FCSTD DOCUMENT  (FreeCAD 0.20R29603 (Git))
Label: layout
License: All rights reserved
LicenseURL: http://en.wikipedia.org/wiki/All_rights_reserved
objects: Sketcher::SketchObject×4, Spreadsheet::Sheet×1
note: 4 computed .brp shape members not serialized (recipe doc carries the construction recipe); baked Part::Feature solids carry a one-line shape summary decoded from their .brp

FEATURE [Spreadsheet::Sheet] Spreadsheet  label="Constants"
  cells = B1=X; C1=Y; D1=Angle; E1=Variance; A2=Far index; C2(FarIndexY)==3 mm; A3=Index; B3(IndexX)==20 mm; C3(IndexY)==8 mm; A4=Ring; B4(RingX)==18 mm; C4(RingY)==10 mm; A5=Far ring; C5(FarRingY)==2 mm; A6=Wide ring; C6(WideRingY)==2 mm; A7=Pinky; B7(PinkyX)==37 mm; C7(PinkyY)==31 mm; A8=Far pinky; B8(FarPinkyX)==35 mm; C8(FarPinkyY)==33 mm; E8(FarPinkyVariance)==1 mm; A9=Thumb; B9(ThumbX)==48 mm; C9(ThumbY)==49 mm; D9(ThumbAngle)==5 deg; A10=LeftThumb; C10(LeftThumbY)==3 mm; D10(LeftThumbAngle)==15 deg; A11=RightThumb; C11(RightThumbY)==3 mm; D11(RightThumbAngle)==15 deg; A12=Numpad; C12(NumpadY)==5 mm; D12(NumpadAngle)==10 deg; B15=Width; C15=Height; A16=Key size; B16(KeyWidth)==18 mm; C16(KeyHeight)==17 mm; A17=Switch hole size; B17(SwitchHoleSize)==14 mm; A18=Edge padding; B18(EdgePaddingWidth)==(KeyWidth - SwitchHoleSize) / 2; C18(EdgePaddingHeight)==1.5 mm; A19=Numpad spacing; B19(NumpadSpacingWidth)==1 mm; C19(NumpadSpacingHeight)==3 mm; A20=Component spacing; B20(ComponentSpacing)==0.5 mm; A21=Corner raidus; B21(CornerRadius)==1 mm; A22=Micro controller size; B22(MicroControllerWidth)==17.78 mm; C22(MicroControllerHeight)==33.02 mm; A23=TRRS size; B23(TRRSWidth)==6.1 mm; C23(TRRSHeight)==12.45 mm; D23(TRRSFullHeight)==100 mm; A24=LED diameter; B24(LEDDiameter)==3.175 mm; A25=Breakaway gap; B25(BreakawayGap)==1 mm; A26=Breakaway width; B26(BreakawayWidth)==8 mm; A27=Breakway margin; B27(BreakawayMargin)==12 mm
FEATURE [Sketcher::SketchObject] Sketch  label="Grid"
  FullyConstrained = true
  expr: Constraints[107] = 2 * Spreadsheet.KeyHeight
  expr: Constraints[108] = <<Constants>>.KeyHeight
  expr: Constraints[109] = Spreadsheet.KeyWidth
  expr: Constraints[10] = 3 * Spreadsheet.KeyHeight
  expr: Constraints[110] = Spreadsheet.KeyWidth
  expr: Constraints[111] = Spreadsheet.FarRingY
  expr: Constraints[112] = Spreadsheet.FarPinkyY
  expr: Constraints[113] = Spreadsheet.FarPinkyX
  expr: Constraints[114] = <<Constants>>.ThumbAngle
  expr: Constraints[122] = <<Constants>>.RightThumbAngle
  expr: Constraints[123] = <<Constants>>.KeyWidth
  expr: Constraints[124] = <<Constants>>.KeyHeight
  expr: Constraints[125] = Spreadsheet.RightThumbY + <<Constants>>.KeyHeight
  expr: Constraints[133] = <<Constants>>.KeyHeight
  expr: Constraints[134] = <<Constants>>.KeyWidth
  expr: Constraints[136] = Spreadsheet.LeftThumbY
  expr: Constraints[137] = <<Constants>>.LeftThumbAngle
  expr: Constraints[147] = <<Constants>>.KeyHeight
  expr: Constraints[148] = <<Constants>>.KeyWidth
  expr: Constraints[156] = <<Constants>>.FarIndexY
  expr: Constraints[157] = Spreadsheet.IndexY
  expr: Constraints[158] = Spreadsheet.IndexX
  expr: Constraints[19] = Spreadsheet.KeyWidth
  expr: Constraints[20] = 3 * Spreadsheet.KeyHeight
  expr: Constraints[28] = Spreadsheet.KeyWidth
  expr: Constraints[29] = 3 * Spreadsheet.KeyHeight
  expr: Constraints[40] = Spreadsheet.KeyWidth
  expr: Constraints[41] = 3 * Spreadsheet.KeyHeight
  expr: Constraints[46] = Spreadsheet.KeyWidth
  expr: Constraints[47] = Spreadsheet.KeyHeight
  expr: Constraints[64] = Spreadsheet.KeyWidth
  expr: Constraints[65] = Spreadsheet.KeyHeight
  expr: Constraints[70] = Spreadsheet.KeyWidth
  expr: Constraints[76] = Spreadsheet.KeyHeight
  expr: Constraints[79] = Spreadsheet.RingY
  expr: Constraints[80] = Spreadsheet.PinkyY
  expr: Constraints[82] = Spreadsheet.ThumbY
  expr: Constraints[83] = Spreadsheet.PinkyX
  expr: Constraints[91] = Spreadsheet.KeyWidth
  expr: Constraints[92] = 2 * <<Constants>>.KeyHeight
  expr: Constraints[94] = Spreadsheet.ThumbX
  expr: Constraints[96] = Spreadsheet.RingX
  expr: Constraints[9] = Spreadsheet.KeyWidth
  sketch-geometry (58):
    g0: LineSegment StartX=-9 StartY=25.5 StartZ=0 EndX=9 EndY=25.5 EndZ=0
    g1: LineSegment StartX=9 StartY=25.5 StartZ=0 EndX=9 EndY=-25.5 EndZ=0
    g2: LineSegment StartX=9 StartY=-25.5 StartZ=0 EndX=-9 EndY=-25.5 EndZ=0
    g3: LineSegment StartX=-9 StartY=-25.5 StartZ=0 EndX=-9 EndY=25.5 EndZ=0
    g4: LineSegment StartX=-11 StartY=17.5 StartZ=0 EndX=-29 EndY=17.5 EndZ=0
    g5: LineSegment StartX=-29 StartY=17.5 StartZ=0 EndX=-29 EndY=-33.5 EndZ=0
    g6: LineSegment StartX=-29 StartY=-33.5 StartZ=0 EndX=-11 EndY=-33.5 EndZ=0
    g7: LineSegment StartX=-11 StartY=-33.5 StartZ=0 EndX=-11 EndY=17.5 EndZ=0
    g8: LineSegment StartX=9 StartY=-35.5 StartZ=0 EndX=9 EndY=15.5 EndZ=0
    g9: LineSegment StartX=9 StartY=15.5 StartZ=0 EndX=27 EndY=15.5 EndZ=0
    g10: LineSegment StartX=27 StartY=15.5 StartZ=0 EndX=27 EndY=-35.5 EndZ=0
    g11: LineSegment StartX=27 StartY=-35.5 StartZ=0 EndX=9 EndY=-35.5 EndZ=0
    g12: GeomPoint X=18 Y=-10 Z=0
    g13: LineSegment StartX=-29 StartY=14.5 StartZ=0 EndX=-47 EndY=14.5 EndZ=0
    g14: LineSegment StartX=-47 StartY=14.5 StartZ=0 EndX=-47 EndY=-36.5 EndZ=0
    g15: LineSegment StartX=-47 StartY=-36.5 StartZ=0 EndX=-29 EndY=-36.5 EndZ=0
    g16: LineSegment StartX=-29 StartY=-36.5 StartZ=0 EndX=-29 EndY=-33.5 EndZ=0
    g17: LineSegment StartX=28 StartY=-22.5 StartZ=0 EndX=28 EndY=-39.5 EndZ=0
    g18: LineSegment StartX=46 StartY=-39.5 StartZ=0 EndX=46 EndY=-22.5 EndZ=0
    g19: LineSegment StartX=46 StartY=-22.5 StartZ=0 EndX=28 EndY=-22.5 EndZ=0
    g20: LineSegment StartX=46 StartY=-41.5 StartZ=0 EndX=64 EndY=-41.5 EndZ=0
    g21: GeomPoint X=37 Y=-31 Z=0
    g22: GeomPoint X=-48 Y=-49 Z=0
    g23: LineSegment StartX=-38.2934 StartY=-56.6833 StartZ=0 EndX=-34.8205 EndY=-36.9871 EndZ=0
    g24: LineSegment StartX=46 StartY=-39.5 StartZ=0 EndX=46 EndY=-41.5 EndZ=0
    g25: GeomPoint X=35 Y=-48 Z=0
    g26: LineSegment StartX=46 StartY=-39.5 StartZ=0 EndX=28 EndY=-39.5 EndZ=0
    g27: LineSegment StartX=28 StartY=-39.5 StartZ=0 EndX=26 EndY=-39.5 EndZ=0
    g28: LineSegment StartX=26 StartY=-39.5 StartZ=0 EndX=26 EndY=-56.5 EndZ=0
    g29: LineSegment StartX=26 StartY=-56.5 StartZ=0 EndX=44 EndY=-56.5 EndZ=0
    g30: LineSegment StartX=44 StartY=-56.5 StartZ=0 EndX=44 EndY=-39.5 EndZ=0
    g31: LineSegment StartX=-38.2934 StartY=-56.6833 StartZ=0 EndX=-56.2249 EndY=-58.2521 EndZ=0
    g32: LineSegment StartX=-56.2249 StartY=-58.2521 StartZ=0 EndX=-57.7066 EndY=-41.3167 EndZ=0
    g33: LineSegment StartX=-57.7066 StartY=-41.3167 StartZ=0 EndX=-39.7751 EndY=-39.7479 EndZ=0
    g34: GeomPoint X=-48 Y=-49 Z=0
    g35: LineSegment StartX=-38.2934 StartY=-56.6833 StartZ=0 EndX=-39.7751 EndY=-39.7479 EndZ=0
    g36: GeomPoint X=55 Y=-33 Z=0
    g37: LineSegment StartX=46 StartY=-22.5 StartZ=0 EndX=46 EndY=-7.5 EndZ=0
    g38: LineSegment StartX=46 StartY=-7.5 StartZ=0 EndX=64 EndY=-7.5 EndZ=0
    g39: LineSegment StartX=64 StartY=-7.5 StartZ=0 EndX=64 EndY=-41.5 EndZ=0
    g40: LineSegment StartX=27 StartY=13.5 StartZ=0 EndX=45 EndY=13.5 EndZ=0
    g41: LineSegment StartX=45 StartY=13.5 StartZ=0 EndX=45 EndY=-20.5 EndZ=0
    g42: LineSegment StartX=45 StartY=-20.5 StartZ=0 EndX=27 EndY=-20.5 EndZ=0
    g43: LineSegment StartX=45 StartY=-7.5 StartZ=0 EndX=63 EndY=-7.5 EndZ=0
    g44: LineSegment StartX=63 StartY=-7.5 StartZ=0 EndX=63 EndY=9.5 EndZ=0
    g45: LineSegment StartX=63 StartY=9.5 StartZ=0 EndX=45 EndY=9.5 EndZ=0
    g46: LineSegment StartX=-34.8205 StartY=-36.9871 StartZ=0 EndX=-17.0939 EndY=-40.1128 EndZ=0
    g47: LineSegment StartX=-17.0939 StartY=-40.1128 StartZ=0 EndX=-20.0459 EndY=-56.8545 EndZ=0
    g48: LineSegment StartX=-20.0459 StartY=-56.8545 StartZ=0 EndX=-37.7725 EndY=-53.7288 EndZ=0
    g49: LineSegment StartX=-61.0132 StartY=-45.0964 StartZ=0 EndX=-55.1989 EndY=-61.0711 EndZ=0
    g50: LineSegment StartX=-55.1989 StartY=-61.0711 StartZ=0 EndX=-72.1133 EndY=-67.2275 EndZ=0
    g51: LineSegment StartX=-72.1133 StartY=-67.2275 StartZ=0 EndX=-77.9277 EndY=-51.2527 EndZ=0
    g52: LineSegment StartX=-77.9277 StartY=-51.2527 StartZ=0 EndX=-61.0132 EndY=-45.0964 EndZ=0
    g53: LineSegment StartX=46 StartY=-41.5 StartZ=0 EndX=44 EndY=-41.5 EndZ=0
    g54: LineSegment StartX=44 StartY=-56.5 StartZ=0 EndX=44 EndY=-58.5 EndZ=0
    g55: LineSegment StartX=44 StartY=-58.5 StartZ=0 EndX=62 EndY=-58.5 EndZ=0
    g56: LineSegment StartX=62 StartY=-58.5 StartZ=0 EndX=62 EndY=-41.5 EndZ=0
    g57: GeomPoint X=64 Y=-24.5 Z=0
  constraints (160):
    c: Coincident(g0,g1)
    c: Coincident(g1,g2)
    c: Coincident(g2,g3)
    c: Coincident(g3,g0)
    c: Horizontal(g0)
    c: Horizontal(g2)
    c: Vertical(g1)
    c: Vertical(g3)
    c: Symmetric(g0,g1,g-1)
    c: Distance(g0) = 18
    c: Distance(g1) = 51
    c: Coincident(g4,g5)
    c: Coincident(g5,g6)
    c: Coincident(g6,g7)
    c: Coincident(g7,g4)
    c: Horizontal(g4)
    c: Horizontal(g6)
    c: Vertical(g5)
    c: Vertical(g7)
    c: Distance(g4) = 18
    c: Distance(g7) = 51
    c: Coincident(g9,g8)
    c: Coincident(g10,g9)
    c: Coincident(g11,g10)
    c: Coincident(g11,g8)
    c: Perpendicular(g8,g9)
    c: Perpendicular(g10,g9)
    c: Perpendicular(g11,g8)
    c: Distance(g9) = 18
    c: Distance(g10) = 51
    c: Symmetric(g8,g10,g12)
    c: PointOnObject(g13,g5)
    c: Horizontal(g13)
    c: Coincident(g14,g13)
    c: Vertical(g14)
    c: Coincident(g15,g14)
    c: Horizontal(g15)
    c: Coincident(g16,g15)
    c: Coincident(g16,g5)
    c: Vertical(g16)
    c: Distance(g13) = 18
    c: Distance(g14) = 51
    c: Coincident(g19,g18)
    c: Coincident(g19,g17)
    c: Perpendicular(g17,g19)
    c: Perpendicular(g18,g19)
    c: Distance(g19) = 18
    c: Distance(g18) = 17
    c: Coincident(g24,g20)
    c: Perpendicular(g20,g24)
    c: Symmetric(g17,g18,g21)
    c: Coincident(g18,g24)
    c: Coincident(g26,g18)
    c: Coincident(g26,g17)
    c: Perpendicular(g26,g18)
    c: Coincident(g27,g17)
    c: Coincident(g28,g27)
    c: Coincident(g29,g28)
    c: Coincident(g30,g29)
    c: PointOnObject(g30,g26)
    c: Perpendicular(g30,g26)
    c: Perpendicular(g29,g30)
    c: Perpendicular(g28,g29)
    c: Perpendicular(g27,g28)
    c: Distance(g29) = 18
    c: Distance(g30) = 17
    c: Symmetric(g27,g29,g25)
    c: Coincident(g32,g31)
    c: Coincident(g33,g32)
    c: Symmetric(g32,g31,g34)
    c: Distance(g33) = 18
    c: Perpendicular(g32,g31)
    c: Coincident(g35,g31)
    c: Coincident(g35,g33)
    c: Perpendicular(g31,g35)
    c: Perpendicular(g33,g32)
    c: Distance(g35) = 17
    c: Coincident(g22,g34)
    c: Coincident(g23,g31)
    c: DistanceY(g12,g-1) = 10
    c: DistanceY(g21,g-1) = 31
    c: Perpendicular(g26,g24)
    c: DistanceY(g22,g-1) = 49
    c: DistanceX(g-1,g21) = 37
    c: Coincident(g37,g18)
    c: Coincident(g38,g37)
    c: Coincident(g39,g38)
    c: Coincident(g39,g20)
    c: Perpendicular(g20,g39)
    c: Perpendicular(g38,g37)
    c: Perpendicular(g39,g38)
    c: Distance(g38) = 18
    c: Distance(g39) = 34
    c: Angle(g17,g-2) = 0
    c: DistanceX(g22,g-1) = 48
    c: Horizontal(g9)
    c: DistanceX(g-1,g12) = 18
    c: PointOnObject(g40,g10)
    c: Coincident(g41,g40)
    c: Coincident(g42,g41)
    c: PointOnObject(g42,g10)
    c: Coincident(g44,g43)
    c: Coincident(g45,g44)
    c: PointOnObject(g45,g41)
    c: Perpendicular(g10,g40)
    c: Perpendicular(g41,g40)
    c: Perpendicular(g42,g41)
    c: Distance(g41) = 34
    c: Distance(g44) = 17
    c: Distance(g40) = 18
    c: Distance(g45) = 18
    c: DistanceY(g40,g9) = 2
    c: DistanceY(g36,g-1) = 33
    c: DistanceX(g-1,g25) = 35
    c: Angle(g-2,g35) = 0.0872665
    c: Coincident(g46,g23)
    c: Coincident(g47,g46)
    c: Coincident(g48,g47)
    c: PointOnObject(g48,g23)
    c: Perpendicular(g46,g23)
    c: Perpendicular(g47,g46)
    c: Perpendicular(g48,g47)
    c: Angle(g23,g35) = 0.261799
    c: Distance(g46) = 18
    c: Distance(g47) = 17
    c: Distance(g23) = 20
    c: Coincident(g50,g49)
    c: Coincident(g51,g50)
    c: Coincident(g52,g51)
    c: Coincident(g52,g49)
    c: Perpendicular(g52,g49)
    c: Perpendicular(g51,g52)
    c: Perpendicular(g50,g49)
    c: Distance(g49) = 17
    c: Distance(g52) = 18
    c: PointOnObject(g31,g49)
    c: Distance(g31,g50) = 3
    c: Angle(g32,g49) = 0.261799
    c: Coincident(g53,g20)
    c: PointOnObject(g53,g30)
    c: Horizontal(g53)
    c: Coincident(g54,g29)
    c: Vertical(g54)
    c: Coincident(g55,g54)
    c: Horizontal(g55)
    c: PointOnObject(g56,g20)
    c: Vertical(g56)
    c: Distance(g56) = 17
    c: Distance(g55) = 18
    c: Coincident(g56,g55)
    c: PointOnObject(g43,g41)
    c: Horizontal(g45)
    c: Horizontal(g43)
    c: Vertical(g44)
    c: Symmetric(g20,g57,g36)
    c: Symmetric(g38,g20,g57)
    c: DistanceY(g13,g4) = 3
    c: DistanceY(g4,g0) = 8
    c: DistanceX(g4,g0) = 20
    c: PointOnObject(g43,g38)
FEATURE [Sketcher::SketchObject] Sketch001  label="Edge"
  FullyConstrained = true
  expr: Constraints[102] = <<Constants>>.KeyWidth + <<Constants>>.EdgePaddingWidth - <<Constants>>.CornerRadius
  expr: Constraints[105] = <<Constants>>.IndexX + 1.5 * <<Constants>>.KeyWidth + <<Constants>>.EdgePaddingWidth
  expr: Constraints[107] = 1.5 * <<Constants>>.KeyHeight - <<Constants>>.IndexY + <<Constants>>.EdgePaddingHeight
  expr: Constraints[11] = <<Constants>>.CornerRadius
  expr: Constraints[12] = <<Constants>>.CornerRadius
  expr: Constraints[13] = <<Constants>>.PinkyX + 1.5 * <<Constants>>.KeyWidth + <<Constants>>.EdgePaddingWidth
  expr: Constraints[16] = <<Constants>>.CornerRadius
  expr: Constraints[17] = <<Constants>>.FarPinkyY + <<Constants>>.FarPinkyVariance + 1.5 * <<Constants>>.KeyHeight + <<Constants>>.EdgePaddingHeight
  expr: Constraints[19] = <<Constants>>.CornerRadius
  expr: Constraints[1] = <<Constants>>.KeyHeight * 1.5 + <<Constants>>.EdgePaddingHeight
  expr: Constraints[23] = Spreadsheet.MicroControllerHeight + 2 * <<Constants>>.ComponentSpacing
  expr: Constraints[24] = <<Constants>>.CornerRadius
  expr: Constraints[28] = <<Constants>>.CornerRadius
  expr: Constraints[32] = <<Constants>>.CornerRadius
  expr: Constraints[37] = <<Constants>>.CornerRadius
  expr: Constraints[3] = <<Constants>>.KeyWidth / 2 + <<Constants>>.EdgePaddingWidth
  expr: Constraints[42] = <<Constants>>.ThumbX
  expr: Constraints[43] = <<Constants>>.ThumbY
  expr: Constraints[45] = <<Constants>>.KeyHeight
  expr: Constraints[46] = <<Constants>>.KeyWidth
  expr: Constraints[47] = <<Constants>>.ThumbAngle
  expr: Constraints[49] = <<Constants>>.LeftThumbAngle
  expr: Constraints[50] = <<Constants>>.LeftThumbY
  expr: Constraints[51] = <<Constants>>.EdgePaddingHeight
  expr: Constraints[52] = <<Constants>>.EdgePaddingHeight
  expr: Constraints[53] = <<Constants>>.KeyHeight
  expr: Constraints[54] = <<Constants>>.CornerRadius
  expr: Constraints[55] = <<Constants>>.CornerRadius
  expr: Constraints[56] = <<Constants>>.CornerRadius
  expr: Constraints[57] = <<Constants>>.CornerRadius
  expr: Constraints[5] = <<Constants>>.KeyWidth / 2 + <<Constants>>.EdgePaddingWidth
  expr: Constraints[65] = <<Constants>>.TRRSHeight + 2 * <<Constants>>.ComponentSpacing
  expr: Constraints[6] = <<Constants>>.CornerRadius
  expr: Constraints[72] = <<Constants>>.CornerRadius
  expr: Constraints[73] = <<Constants>>.CornerRadius
  expr: Constraints[76] = <<Constants>>.CornerRadius
  expr: Constraints[83] = Spreadsheet.BreakawayMargin - Spreadsheet.BreakawayGap / 2 - <<Constants>>.CornerRadius
  expr: Constraints[84] = Spreadsheet.BreakawayMargin - Spreadsheet.BreakawayGap / 2 - <<Constants>>.CornerRadius
  expr: Constraints[87] = Spreadsheet.BreakawayWidth + Spreadsheet.BreakawayGap
  expr: Constraints[88] = Spreadsheet.BreakawayWidth + Spreadsheet.BreakawayGap
  expr: Constraints[95] = <<Constants>>.MicroControllerWidth + 2 * <<Constants>>.ComponentSpacing
  expr: Constraints[97] = <<Constants>>.TRRSWidth + <<Constants>>.ComponentSpacing
  sketch-geometry (42):
    g0: LineSegment StartX=10 StartY=27 StartZ=0 EndX=-10 EndY=27 EndZ=0
    g1: LineSegment StartX=-11 StartY=20 StartZ=0 EndX=-11 EndY=26 EndZ=0
    g2: LineSegment StartX=11 StartY=26 StartZ=0 EndX=11 EndY=20 EndZ=0
    g3: ArcOfCircle CenterX=-10 CenterY=26 CenterZ=0 NormalX=0 NormalY=0 NormalZ=1 AngleXU=0 Radius=1 StartAngle=1.5708 EndAngle=3.14159
    g4: ArcOfCircle CenterX=10 CenterY=26 CenterZ=0 NormalX=0 NormalY=0 NormalZ=1 AngleXU=0 Radius=1 StartAngle=4e-16 EndAngle=1.5708
    g5: ArcOfCircle CenterX=65 CenterY=18 CenterZ=0 NormalX=0 NormalY=0 NormalZ=1 AngleXU=0 Radius=1 StartAngle=0 EndAngle=1.5708
    g6: LineSegment StartX=65 StartY=-61 StartZ=0 EndX=-50.4414 EndY=-61 EndZ=0
    g7: ArcOfCircle CenterX=65 CenterY=-60 CenterZ=0 NormalX=0 NormalY=0 NormalZ=1 AngleXU=0 Radius=1 StartAngle=4.71239 EndAngle=6.28319
    g8: ArcOfCircle CenterX=-48 CenterY=18 CenterZ=0 NormalX=0 NormalY=0 NormalZ=1 AngleXU=0 Radius=1 StartAngle=1.5708 EndAngle=3.14159
    g9: LineSegment StartX=-48 StartY=19 StartZ=0 EndX=-73.38 EndY=19 EndZ=0
    g10: LineSegment StartX=-50 StartY=-15.02 StartZ=0 EndX=-66.78 EndY=-15.02 EndZ=0
    g11: ArcOfCircle CenterX=-66.78 CenterY=-16.02 CenterZ=0 NormalX=0 NormalY=0 NormalZ=1 AngleXU=0 Radius=1 StartAngle=1.5708 EndAngle=3.14159
    g12: LineSegment StartX=-48 StartY=19 StartZ=0 EndX=-12 EndY=19 EndZ=0
    g13: ArcOfCircle CenterX=-12 CenterY=20 CenterZ=0 NormalX=0 NormalY=0 NormalZ=1 AngleXU=0 Radius=1 StartAngle=4.71239 EndAngle=6.28319
    g14: LineSegment StartX=65 StartY=19 StartZ=0 EndX=12 EndY=19 EndZ=0
    g15: ArcOfCircle CenterX=12 CenterY=20 CenterZ=0 NormalX=0 NormalY=0 NormalZ=1 AngleXU=0 Radius=1 StartAngle=3.14159 EndAngle=4.71239
    g16: ArcOfCircle CenterX=-50 CenterY=-14.02 CenterZ=0 NormalX=0 NormalY=0 NormalZ=1 AngleXU=0 Radius=1 StartAngle=4.71239 EndAngle=6.28319
    g17: LineSegment StartX=-49 StartY=-14.02 StartZ=0 EndX=-49 EndY=18 EndZ=0
    g18: GeomPoint X=-48 Y=-49 Z=0
    g19: LineSegment StartX=-57.7066 StartY=-41.3167 StartZ=0 EndX=-56.2249 EndY=-58.2521 EndZ=0
    g20: LineSegment StartX=-56.2249 StartY=-58.2521 StartZ=0 EndX=-38.2934 EndY=-56.6833 EndZ=0
    g21: LineSegment StartX=-61.5262 StartY=-43.6868 StartZ=0 EndX=-54.6858 EndY=-62.4807 EndZ=0
    g22: GeomPoint X=-55.1989 Y=-61.0711 Z=0
    g23: GeomPoint X=-61.0132 Y=-45.0964 Z=0
    g24: ArcOfCircle CenterX=-68.78 CenterY=-45.2628 CenterZ=0 NormalX=0 NormalY=0 NormalZ=1 AngleXU=0 Radius=1 StartAngle=5.06145 EndAngle=6.28319
    g25: ArcOfCircle CenterX=-68.78 CenterY=4.55 CenterZ=0 NormalX=0 NormalY=0 NormalZ=1 AngleXU=0 Radius=1 StartAngle=0 EndAngle=1.5708
    g26: ArcOfCircle CenterX=-73.38 CenterY=6.55 CenterZ=0 NormalX=0 NormalY=0 NormalZ=1 AngleXU=0 Radius=1 StartAngle=3.14159 EndAngle=4.71239
    g27: ArcOfCircle CenterX=-73.38 CenterY=18 CenterZ=0 NormalX=0 NormalY=0 NormalZ=1 AngleXU=0 Radius=1 StartAngle=1.5708 EndAngle=3.14159
    g28: LineSegment StartX=-68.78 StartY=5.55 StartZ=0 EndX=-73.38 EndY=5.55 EndZ=0
    g29: LineSegment StartX=-74.38 StartY=6.55 StartZ=0 EndX=-74.38 EndY=18 EndZ=0
    g30: ArcOfCircle CenterX=-79.0384 CenterY=-51.1249 CenterZ=0 NormalX=0 NormalY=0 NormalZ=1 AngleXU=0 Radius=1 StartAngle=1.91986 EndAngle=3.49066
    g31: LineSegment StartX=-79.9781 StartY=-51.4669 StartZ=0 EndX=-73.8217 EndY=-68.3814 EndZ=0
    g32: ArcOfCircle CenterX=-72.882 CenterY=-68.0394 CenterZ=0 NormalX=0 NormalY=0 NormalZ=1 AngleXU=0 Radius=1 StartAngle=3.49066 EndAngle=5.06145
    g33: ArcOfCircle CenterX=-50.4414 CenterY=-62 CenterZ=0 NormalX=0 NormalY=0 NormalZ=1 AngleXU=0 Radius=1 StartAngle=1.5708 EndAngle=1.91986
    g34: LineSegment StartX=-50.7834 StartY=-61.0603 StartZ=0 EndX=-72.54 EndY=-68.9791 EndZ=0
    g35: LineSegment StartX=66 StartY=-60 StartZ=0 EndX=66 EndY=-49.5 EndZ=0
    g36: LineSegment StartX=66 StartY=18 StartZ=0 EndX=66 EndY=7.5 EndZ=0
    g37: LineSegment StartX=66 StartY=-1.5 StartZ=0 EndX=66 EndY=-40.5 EndZ=0
    g38: LineSegment StartX=-67.78 StartY=-16.02 StartZ=0 EndX=-67.78 EndY=-45.2628 EndZ=0
    g39: LineSegment StartX=-68.438 StartY=-46.2025 StartZ=0 EndX=-79.3804 EndY=-50.1852 EndZ=0
    g40: LineSegment StartX=-67.78 StartY=4.55 StartZ=0 EndX=-67.78 EndY=-16.02 EndZ=0
    g41: LineSegment StartX=-61.5262 StartY=-43.6868 StartZ=0 EndX=-68.438 EndY=-46.2025 EndZ=0
  constraints (108):
    c: Horizontal(g0)
    c: DistanceY(g-1,g0) = 27
    c: Vertical(g1)
    c: DistanceX(g1,g-1) = 11
    c: Vertical(g2)
    c: DistanceX(g-1,g2) = 11
    c: Radius(g3) = 1
    c: Tangent(g3,g1) = 1.5708
    c: Tangent(g3,g0) = -1.5708
    c: Tangent(g4,g0) = -1.5708
    c: Tangent(g4,g2) = 1.5708
    c: Radius(g4) = 1
    c: Radius(g5) = 1
    c: DistanceX(g-1,g5) = 66
    c: Horizontal(g6)
    c: Tangent(g7,g6) = 1.5708
    c: Radius(g7) = 1
    c: DistanceY(g6,g-1) = 61
    c: Coincident(g8,g9) = -1.5708
    c: Radius(g8) = 1
    c: Horizontal(g9)
    c: Horizontal(g10)
    c: Tangent(g11,g10) = -1.5708
    c: DistanceY(g10,g9) = 34.02
    c: Radius(g11) = 1
    c: Horizontal(g12)
    c: Tangent(g12,g8) = 1.5708
    c: Tangent(g13,g1) = -1.5708
    c: Radius(g13) = 1
    c: Horizontal(g14)
    c: Tangent(g15,g14) = 1.5708
    c: Tangent(g15,g2) = -1.5708
    c: Radius(g15) = 1
    c: Tangent(g17,g8) = 1.5708
    c: Tangent(g17,g16) = -1.5708
    c: Tangent(g16,g10) = 1.5708
    c: Vertical(g17)
    c: Radius(g16) = 1
    c: Coincident(g20,g19)
    c: PointOnObject(g19,g21)
    c: PointOnObject(g22,g21)
    c: Symmetric(g19,g20,g18)
    c: DistanceX(g18,g-1) = 48
    c: DistanceY(g18,g-1) = 49
    c: Perpendicular(g19,g20)
    c: Distance(g19) = 17
    c: Distance(g20) = 18
    c: Angle(g-2,g19) = 0.0872665
    c: PointOnObject(g23,g21)
    c: Angle(g19,g21) = 0.261799
    c: Distance(g22,g19) = 3
    c: Distance(g21,g22) = 1.5
    c: Distance(g23,g21) = 1.5
    c: Distance(g23,g22) = 17
    c: Radius(g24) = 1
    c: Radius(g27) = 1
    c: Radius(g26) = 1
    c: Radius(g25) = 1
    c: Tangent(g27,g9) = -1.5708
    c: Tangent(g29,g27) = 1.5708
    c: Tangent(g29,g26) = 1.5708
    c: Tangent(g28,g26) = 1.5708
    c: Tangent(g28,g25) = -1.5708
    c: Horizontal(g28)
    c: Vertical(g29)
    c: DistanceY(g26,g9) = 13.45
    c: PointOnObject(g21,g34)
    c: Tangent(g33,g6) = -1.5708
    c: Tangent(g34,g33) = -1.5708
    c: Tangent(g34,g32) = 1.5708
    c: Tangent(g32,g31) = -1.5708
    c: Tangent(g31,g30) = -1.5708
    c: Radius(g30) = 1
    c: Radius(g32) = 1
    c: Perpendicular(g21,g34)
    c: Perpendicular(g31,g34)
    c: Radius(g33) = 1
    c: Tangent(g14,g5) = -1.5708
    c: Vertical(g7,g5)
    c: Vertical(g35)
    c: Vertical(g36)
    c: Tangent(g36,g5) = 1.5708
    c: Tangent(g35,g7) = -1.5708
    c: Distance(g35) = 10.5
    c: Distance(g36) = 10.5
    c: Vertical(g37)
    c: Vertical(g37,g36)
    c: Distance(g37,g36) = 9
    c: Distance(g37,g35) = 9
    c: Coincident(g38,g11)
    c: Coincident(g39,g24)
    c: Vertical(g40)
    c: Tangent(g40,g11) = -1.5708
    c: Vertical(g38)
    c: Tangent(g38,g24) = 1.5708
    c: DistanceX(g11,g16) = 18.78
    c: Tangent(g40,g25) = 1.5708
    c: DistanceX(g26,g25) = 6.6
    c: Coincident(g41,g21)
    c: Perpendicular(g41,g21)
    c: Parallel(g41,g39)
    c: Tangent(g41,g24) = 1.5708
    c: Distance(g21,g30) = 19
    c: Tangent(g30,g39) = -1.5708
    c: Tangent(g13,g12) = -1.5708
    c: DistanceX(g8,g-1) = 49
    c: Horizontal(g12,g14)
    c: DistanceY(g-1,g12) = 19
FEATURE [Sketcher::SketchObject] Sketch002  label="EdgeNumpad"
  FullyConstrained = true
  expr: Constraints[0] = <<Constants>>.CornerRadius
  expr: Constraints[102] = <<Constants>>.EdgePaddingHeight
  expr: Constraints[103] = <<Constants>>.EdgePaddingWidth
  expr: Constraints[108] = <<Constants>>.FarPinkyY + 1.5 * <<Constants>>.KeyHeight + <<Constants>>.FarPinkyVariance + <<Constants>>.EdgePaddingHeight
  expr: Constraints[10] = Spreadsheet.BreakawayGap
  expr: Constraints[12] = Spreadsheet.BreakawayGap
  expr: Constraints[13] = Spreadsheet.BreakawayMargin - Spreadsheet.BreakawayGap / 2
  expr: Constraints[14] = Spreadsheet.BreakawayWidth + Spreadsheet.BreakawayGap
  expr: Constraints[15] = Spreadsheet.BreakawayWidth + Spreadsheet.BreakawayGap
  expr: Constraints[16] = <<Constants>>.PinkyX + 1.5 * <<Constants>>.KeyWidth + <<Constants>>.EdgePaddingWidth + Spreadsheet.BreakawayGap
  expr: Constraints[1] = <<Constants>>.CornerRadius
  expr: Constraints[28] = 3 * <<Constants>>.KeyWidth + 2 * <<Constants>>.NumpadSpacingWidth
  expr: Constraints[2] = <<Constants>>.KeyHeight * 1.5 + <<Constants>>.EdgePaddingHeight - <<Constants>>.IndexY
  expr: Constraints[32] = <<Constants>>.NumpadAngle
  expr: Constraints[33] = 4 * <<Constants>>.KeyHeight + <<Constants>>.NumpadSpacingHeight
  expr: Constraints[3] = <<Constants>>.CornerRadius
  expr: Constraints[41] = <<Constants>>.CornerRadius
  expr: Constraints[46] = <<Constants>>.CornerRadius
  expr: Constraints[4] = <<Constants>>.CornerRadius
  expr: Constraints[53] = <<Constants>>.CornerRadius
  expr: Constraints[62] = <<Constants>>.EdgePaddingHeight
  expr: Constraints[63] = <<Constants>>.EdgePaddingWidth
  expr: Constraints[69] = <<Constants>>.EdgePaddingHeight
  expr: Constraints[6] = Spreadsheet.BreakawayGap
  expr: Constraints[76] = <<Constants>>.CornerRadius
  expr: Constraints[77] = <<Constants>>.CornerRadius
  expr: Constraints[78] = Spreadsheet.BreakawayMargin - Spreadsheet.BreakawayGap / 2
  expr: Constraints[80] = <<Constants>>.CornerRadius
  expr: Constraints[84] = <<Constants>>.EdgePaddingWidth
  expr: Constraints[8] = Spreadsheet.BreakawayGap
  expr: Constraints[93] = <<Constants>>.CornerRadius
  expr: Constraints[94] = <<Constants>>.CornerRadius
  expr: Constraints[95] = <<Constants>>.CornerRadius
  sketch-geometry (42):
    g0: ArcOfCircle CenterX=130.217 CenterY=18 CenterZ=0 NormalX=0 NormalY=0 NormalZ=1 AngleXU=0 Radius=1 StartAngle=8e-16 EndAngle=1.5708
    g1: ArcOfCircle CenterX=68 CenterY=18 CenterZ=0 NormalX=0 NormalY=0 NormalZ=1 AngleXU=0 Radius=1 StartAngle=1.5708 EndAngle=3.14159
    g2: ArcOfCircle CenterX=68 CenterY=-60 CenterZ=0 NormalX=0 NormalY=0 NormalZ=1 AngleXU=0 Radius=1 StartAngle=3.14159 EndAngle=4.71239
    g3: ArcOfCircle CenterX=130.217 CenterY=-60 CenterZ=0 NormalX=0 NormalY=0 NormalZ=1 AngleXU=0 Radius=1 StartAngle=4.71239 EndAngle=6.28319
    g4: ArcOfCircle CenterX=66.5 CenterY=7.5 CenterZ=0 NormalX=0 NormalY=0 NormalZ=1 AngleXU=0 Radius=0.5 StartAngle=3.14159 EndAngle=6.28319
    g5: ArcOfCircle CenterX=66.5 CenterY=-1.5 CenterZ=0 NormalX=0 NormalY=0 NormalZ=1 AngleXU=0 Radius=0.5 StartAngle=0 EndAngle=3.14159
    g6: ArcOfCircle CenterX=66.5 CenterY=-49.5 CenterZ=0 NormalX=0 NormalY=0 NormalZ=1 AngleXU=0 Radius=0.5 StartAngle=2.4e-15 EndAngle=3.14159
    g7: ArcOfCircle CenterX=66.5 CenterY=-40.5 CenterZ=0 NormalX=0 NormalY=0 NormalZ=1 AngleXU=0 Radius=0.5 StartAngle=3.14159 EndAngle=6.28319
    g8: LineSegment StartX=67 StartY=18 StartZ=0 EndX=67 EndY=7.5 EndZ=0
    g9: LineSegment StartX=67 StartY=-1.5 StartZ=0 EndX=67 EndY=-40.5 EndZ=0
    g10: LineSegment StartX=67 StartY=-49.5 StartZ=0 EndX=67 EndY=-60 EndZ=0
    g11: LineSegment StartX=79.329 StartY=18.8228 StartZ=0 EndX=134.478 EndY=9.09853 EndZ=0
    g12: LineSegment StartX=79.329 StartY=18.8228 StartZ=0 EndX=67 EndY=-51.0985 EndZ=0
    g13: GeomPoint X=100.739 Y=-21 Z=0
    g14: GeomPoint X=99.1087 Y=-21 Z=0
    g15: LineSegment StartX=134.478 StartY=9.09853 StartZ=0 EndX=122.149 EndY=-60.8228 EndZ=0
    g16: LineSegment StartX=122.149 StartY=-60.8228 StartZ=0 EndX=67 EndY=-51.0985 EndZ=0
    g17: LineSegment StartX=131.217 StartY=-60 StartZ=0 EndX=131.217 EndY=-21 EndZ=0
    g18: LineSegment StartX=136.535 StartY=9.24363 StartZ=0 EndX=131.233 EndY=-20.8264 EndZ=0
    g19: ArcOfCircle CenterX=135.55 CenterY=9.41728 CenterZ=0 NormalX=0 NormalY=0 NormalZ=1 AngleXU=0 Radius=1 StartAngle=6.10865 EndAngle=7.67945
    g20: ArcOfCircle CenterX=132.217 CenterY=-21 CenterZ=0 NormalX=0 NormalY=0 NormalZ=1 AngleXU=0 Radius=1 StartAngle=2.96706 EndAngle=3.14159
    g21: LineSegment StartX=135.724 StartY=10.4021 StartZ=0 EndX=132.044 EndY=11.0509 EndZ=0
    g22: LineSegment StartX=131.217 StartY=18 StartZ=0 EndX=131.217 EndY=12.0358 EndZ=0
    g23: ArcOfCircle CenterX=132.217 CenterY=12.0358 CenterZ=0 NormalX=0 NormalY=0 NormalZ=1 AngleXU=0 Radius=1 StartAngle=3.14159 EndAngle=4.53786
    g24: GeomPoint X=134.739 Y=10.5757 Z=0
    g25: GeomPoint X=136.448 Y=8.75123 Z=0
    g26: LineSegment StartX=86.8762 StartY=19.0152 StartZ=0 EndX=78.6012 EndY=20.4743 EndZ=0
    g27: ArcOfCircle CenterX=78.4276 CenterY=19.4895 CenterZ=0 NormalX=0 NormalY=0 NormalZ=1 AngleXU=0 Radius=1 StartAngle=1.39626 EndAngle=2.88348
    g28: GeomPoint X=79.5895 Y=20.3 Z=0
    g29: ArcOfCircle CenterX=87.0499 CenterY=20 CenterZ=0 NormalX=0 NormalY=0 NormalZ=1 AngleXU=0 Radius=1 StartAngle=4.53786 EndAngle=4.71239
    g30: LineSegment StartX=68 StartY=19 StartZ=0 EndX=76.4939 EndY=19 EndZ=0
    g31: LineSegment StartX=87.0499 StartY=19 StartZ=0 EndX=130.217 EndY=19 EndZ=0
    g32: ArcOfCircle CenterX=76.4939 CenterY=20 CenterZ=0 NormalX=0 NormalY=0 NormalZ=1 AngleXU=0 Radius=1 StartAngle=4.71239 EndAngle=6.02507
    g33: LineSegment StartX=77.4607 StartY=19.7447 StartZ=0 EndX=79.4303 EndY=19.3974 EndZ=0
    g34: LineSegment StartX=68 StartY=-61 StartZ=0 EndX=114.428 EndY=-61 EndZ=0
    g35: LineSegment StartX=130.217 StartY=-61 StartZ=0 EndX=124.984 EndY=-61 EndZ=0
    g36: LineSegment StartX=114.602 StartY=-61.0152 StartZ=0 EndX=122.877 EndY=-62.4743 EndZ=0
    g37: ArcOfCircle CenterX=124.984 CenterY=-62 CenterZ=0 NormalX=0 NormalY=0 NormalZ=1 AngleXU=0 Radius=1 StartAngle=1.5708 EndAngle=2.88348
    g38: ArcOfCircle CenterX=123.051 CenterY=-61.4895 CenterZ=0 NormalX=0 NormalY=0 NormalZ=1 AngleXU=0 Radius=1 StartAngle=4.53786 EndAngle=6.02507
    g39: ArcOfCircle CenterX=114.428 CenterY=-62 CenterZ=0 NormalX=0 NormalY=0 NormalZ=1 AngleXU=0 Radius=1 StartAngle=1.39626 EndAngle=1.5708
    g40: LineSegment StartX=124.018 StartY=-61.7447 StartZ=0 EndX=122.048 EndY=-61.3974 EndZ=0
    g41: GeomPoint X=121.889 Y=-62.3 Z=0
  constraints (109):
    c: Radius(g0) = 1
    c: Radius(g1) = 1
    c: DistanceY(g-1,g1) = 19
    c: Radius(g3) = 1
    c: Radius(g2) = 1
    c: Horizontal(g4,g4)
    c: Diameter(g4) = 1
    c: Horizontal(g5,g5)
    c: Diameter(g5) = 1
    c: Horizontal(g6,g6)
    c: Diameter(g6) = 1
    c: Horizontal(g7,g7)
    c: Diameter(g7) = 1
    c: DistanceY(g2,g6) = 11.5
    c: DistanceY(g5,g4) = 9
    c: DistanceY(g6,g7) = 9
    c: DistanceX(g-1,g1) = 67
    c: Vertical(g8)
    c: Tangent(g8,g1) = -1.5708
    c: Tangent(g8,g4) = 1.5708
    c: Vertical(g9)
    c: Tangent(g9,g5) = 1.5708
    c: Tangent(g9,g7) = 1.5708
    c: Vertical(g4,g5)
    c: Vertical(g7,g6)
    c: Vertical(g10)
    c: Tangent(g10,g2) = -1.5708
    c: Tangent(g10,g6) = 1.5708
    c: Distance(g11) = 56
    c: Coincident(g12,g11)
    c: PointOnObject(g12,g10)
    c: Perpendicular(g12,g11)
    c: Angle(g12,g8) = 0.174533
    c: Distance(g12) = 71
    c: Symmetric(g11,g12,g13)
    c: Horizontal(g14,g13)
    c: Coincident(g15,g11)
    c: Coincident(g16,g15)
    c: Coincident(g16,g12)
    c: Perpendicular(g16,g12)
    c: Perpendicular(g16,g15)
    c: Radius(g19) = 1
    c: Vertical(g17)
    c: Horizontal(g17,g14)
    c: Tangent(g20,g18) = -1.5708
    c: Tangent(g20,g17) = 1.5708
    c: Radius(g20) = 1
    c: Tangent(g17,g3) = -1.5708
    c: Vertical(g22)
    c: Perpendicular(g21,g15)
    c: Tangent(g21,g19) = -1.5708
    c: Tangent(g23,g22) = -1.5708
    c: Tangent(g23,g21) = 1.5708
    c: Radius(g23) = 1
    c: Vertical(g22,g17)
    c: Tangent(g22,g0) = 1.5708
    c: Tangent(g18,g19) = 1.5708
    c: Perpendicular(g11,g18)
    c: PointOnObject(g24,g21)
    c: PointOnObject(g25,g18)
    c: PointOnObject(g24,g15)
    c: PointOnObject(g25,g11)
    c: Distance(g24,g11) = 1.5
    c: Distance(g25,g11) = 2
    c: Perpendicular(g12,g26)
    c: PointOnObject(g28,g26)
    c: Tangent(g27,g26) = -1.5708
    c: Tangent(g29,g26) = 1.5708
    c: PointOnObject(g28,g12)
    c: Distance(g11,g28) = 1.5
    c: Horizontal(g30)
    c: Horizontal(g31)
    c: Tangent(g30,g1) = 1.5708
    c: Tangent(g31,g29) = -1.5708
    c: Tangent(g31,g0) = 1.5708
    c: Symmetric(g1,g3,g14)
    c: Radius(g27) = 1
    c: Radius(g29) = 1
    c: DistanceY(g4,g1) = 11.5
    c: Tangent(g32,g30) = -1.5708
    c: Radius(g32) = 1
    c: Coincident(g33,g32)
    c: PointOnObject(g33,g12)
    c: Perpendicular(g12,g33)
    c: Distance(g33) = 2
    c: Horizontal(g29,g30)
    c: Horizontal(g34)
    c: Horizontal(g35)
    c: Tangent(g39,g34) = 1.5708
    c: Tangent(g39,g36) = 1.5708
    c: Tangent(g38,g36) = -1.5708
    c: Coincident(g37,g40) = -1.5708
    c: Tangent(g37,g35) = -1.5708
    c: Radius(g37) = 1
    c: Radius(g38) = 1
    c: Radius(g39) = 1
    c: Horizontal(g34,g35)
    c: PointOnObject(g40,g15)
    c: Perpendicular(g36,g15)
    c: PointOnObject(g41,g36)
    c: PointOnObject(g41,g15)
    c: Perpendicular(g15,g40)
    c: Distance(g41,g15) = 1.5
    c: Distance(g40) = 2
    c: Tangent(g34,g2) = -1.5708
    c: Tangent(g35,g3) = 1.5708
    c: Tangent(g27,g32) = 1.5708
    c: Tangent(g38,g37) = 1.5708
    c: DistanceY(g2,g-1) = 61
FEATURE [Sketcher::SketchObject] Sketch003  label="Components"
  FullyConstrained = true
  expr: Constraints[100] = <<Constants>>.KeyWidth
  expr: Constraints[101] = <<Constants>>.KeyWidth
  expr: Constraints[102] = <<Constants>>.KeyWidth
  expr: Constraints[103] = <<Constants>>.KeyHeight
  expr: Constraints[104] = <<Constants>>.KeyHeight
  expr: Constraints[105] = <<Constants>>.KeyHeight + <<Constants>>.RightThumbY
  expr: Constraints[106] = <<Constants>>.LeftThumbY
  expr: Constraints[107] = <<Constants>>.RightThumbY
  expr: Constraints[108] = <<Constants>>.ThumbAngle
  expr: Constraints[109] = <<Constants>>.RightThumbAngle
  expr: Constraints[110] = <<Constants>>.LeftThumbAngle
  expr: Constraints[128] = 2 * (<<Constants>>.KeyWidth + <<Constants>>.NumpadSpacingWidth)
  expr: Constraints[129] = <<Constants>>.NumpadAngle
  expr: Constraints[130] = <<Constants>>.KeyHeight * 3 + <<Constants>>.NumpadSpacingHeight
  expr: Constraints[131] = <<Constants>>.KeyHeight
  expr: Constraints[132] = <<Constants>>.KeyHeight
  expr: Constraints[133] = <<Constants>>.KeyHeight
  expr: Constraints[134] = <<Constants>>.KeyHeight
  expr: Constraints[135] = <<Constants>>.KeyHeight
  expr: Constraints[136] = <<Constants>>.KeyHeight
  expr: Constraints[145] = <<Constants>>.KeyHeight
  expr: Constraints[146] = <<Constants>>.KeyWidth
  expr: Constraints[148] = <<Constants>>.KeyWidth / 2 + <<Constants>>.EdgePaddingWidth + Spreadsheet.BreakawayGap
  expr: Constraints[149] = <<Constants>>.KeyHeight * 1.5 - <<Constants>>.IndexY + <<Constants>>.EdgePaddingHeight - <<Constants>>.ComponentSpacing
  expr: Constraints[150] = (<<Constants>>.KeyHeight - <<Constants>>.IndexY + <<Constants>>.FarPinkyY + <<Constants>>.FarPinkyVariance) / 2
  expr: Constraints[152] = <<Constants>>.KeyHeight
  expr: Constraints[153] = <<Constants>>.KeyHeight
  expr: Constraints[154] = <<Constants>>.KeyWidth
  expr: Constraints[53] = <<Constants>>.KeyHeight
  expr: Constraints[54] = <<Constants>>.KeyHeight
  expr: Constraints[55] = <<Constants>>.KeyHeight
  expr: Constraints[56] = <<Constants>>.KeyHeight
  expr: Constraints[57] = <<Constants>>.KeyHeight
  expr: Constraints[58] = <<Constants>>.KeyHeight
  expr: Constraints[59] = <<Constants>>.KeyHeight
  expr: Constraints[5] = <<Constants>>.KeyHeight
  expr: Constraints[60] = <<Constants>>.KeyHeight
  expr: Constraints[61] = <<Constants>>.KeyHeight
  expr: Constraints[62] = <<Constants>>.KeyWidth
  expr: Constraints[63] = <<Constants>>.KeyWidth
  expr: Constraints[64] = <<Constants>>.RingX
  expr: Constraints[65] = <<Constants>>.IndexX
  expr: Constraints[66] = <<Constants>>.KeyWidth
  expr: Constraints[67] = <<Constants>>.IndexY
  expr: Constraints[68] = <<Constants>>.FarIndexY
  expr: Constraints[69] = <<Constants>>.RingY
  expr: Constraints[6] = <<Constants>>.KeyHeight
  expr: Constraints[70] = <<Constants>>.FarRingY
  expr: Constraints[71] = <<Constants>>.KeyWidth
  expr: Constraints[72] = <<Constants>>.PinkyX
  expr: Constraints[73] = <<Constants>>.PinkyY
  expr: Constraints[74] = <<Constants>>.FarPinkyY
  expr: Constraints[75] = <<Constants>>.FarPinkyX
  expr: Constraints[76] = <<Constants>>.KeyWidth / 2 + <<Constants>>.EdgePaddingWidth + <<Constants>>.ComponentSpacing
  expr: Constraints[77] = <<Constants>>.MicroControllerWidth / 2
  expr: Constraints[78] = <<Constants>>.MicroControllerHeight / 2 - <<Constants>>.TRRSHeight / 2
  expr: Constraints[79] = <<Constants>>.MicroControllerWidth / 2 + <<Constants>>.ComponentSpacing + <<Constants>>.TRRSWidth / 2
  expr: Constraints[82] = 2 * <<Constants>>.LEDDiameter
  expr: Constraints[83] = 2 * <<Constants>>.LEDDiameter
  expr: Constraints[85] = <<Constants>>.MicroControllerHeight / 2
  expr: Constraints[86] = (<<Constants>>.MicroControllerHeight + <<Constants>>.MicroControllerWidth) / 2 + 2 * <<Constants>>.ComponentSpacing - 2 * <<Constants>>.LEDDiameter
  expr: Constraints[87] = <<Constants>>.ThumbX
  expr: Constraints[88] = <<Constants>>.ThumbY
  sketch-geometry (56):
    g0: Circle CenterX=-49.5 CenterY=18.5 CenterZ=0 NormalX=0 NormalY=0 NormalZ=1 AngleXU=0 Radius=0.25
    g1: Circle CenterX=0 CenterY=0 CenterZ=0 NormalX=0 NormalY=0 NormalZ=1 AngleXU=0 Radius=0.56
    g2: Circle CenterX=0 CenterY=17 CenterZ=0 NormalX=0 NormalY=0 NormalZ=1 AngleXU=0 Radius=0.51
    g3: Circle CenterX=0 CenterY=-17 CenterZ=0 NormalX=0 NormalY=0 NormalZ=1 AngleXU=0 Radius=0.61
    g4: Circle CenterX=-20 CenterY=9 CenterZ=0 NormalX=0 NormalY=0 NormalZ=1 AngleXU=0 Radius=0.505
    g5: Circle CenterX=-20 CenterY=-8 CenterZ=0 NormalX=0 NormalY=0 NormalZ=1 AngleXU=0 Radius=0.555
    g6: Circle CenterX=-20 CenterY=-25 CenterZ=0 NormalX=0 NormalY=0 NormalZ=1 AngleXU=0 Radius=0.605
    g7: Circle CenterX=-38 CenterY=6 CenterZ=0 NormalX=0 NormalY=0 NormalZ=1 AngleXU=0 Radius=0.5
    g8: Circle CenterX=-38 CenterY=-11 CenterZ=0 NormalX=0 NormalY=0 NormalZ=1 AngleXU=0 Radius=0.55
    g9: Circle CenterX=-38 CenterY=-28 CenterZ=0 NormalX=0 NormalY=0 NormalZ=1 AngleXU=0 Radius=0.6
    g10: Circle CenterX=-58.39 CenterY=1.99 CenterZ=0 NormalX=0 NormalY=0 NormalZ=1 AngleXU=0 Radius=0.35
    g11: Circle CenterX=-70.83 CenterY=12.275 CenterZ=0 NormalX=0 NormalY=0 NormalZ=1 AngleXU=0 Radius=0.3
    g12: Circle CenterX=18 CenterY=7 CenterZ=0 NormalX=0 NormalY=0 NormalZ=1 AngleXU=0 Radius=0.515
    g13: Circle CenterX=18 CenterY=-10 CenterZ=0 NormalX=0 NormalY=0 NormalZ=1 AngleXU=0 Radius=0.565
    g14: Circle CenterX=18 CenterY=-27 CenterZ=0 NormalX=0 NormalY=0 NormalZ=1 AngleXU=0 Radius=0.615
    g15: Circle CenterX=36 CenterY=-12 CenterZ=0 NormalX=0 NormalY=0 NormalZ=1 AngleXU=0 Radius=0.57
    g16: Circle CenterX=36 CenterY=5 CenterZ=0 NormalX=0 NormalY=0 NormalZ=1 AngleXU=0 Radius=0.52
    g17: Circle CenterX=54 CenterY=1 CenterZ=0 NormalX=0 NormalY=0 NormalZ=1 AngleXU=0 Radius=0.525
    g18: Circle CenterX=55 CenterY=-16 CenterZ=0 NormalX=0 NormalY=0 NormalZ=1 AngleXU=0 Radius=0.575
    g19: Circle CenterX=37 CenterY=-31 CenterZ=0 NormalX=0 NormalY=0 NormalZ=1 AngleXU=0 Radius=0.62
    g20: Circle CenterX=55 CenterY=-33 CenterZ=0 NormalX=0 NormalY=0 NormalZ=1 AngleXU=0 Radius=0.625
    g21: Circle CenterX=53 CenterY=-50 CenterZ=0 NormalX=0 NormalY=0 NormalZ=1 AngleXU=0 Radius=0.675
    g22: Circle CenterX=35 CenterY=-48 CenterZ=0 NormalX=0 NormalY=0 NormalZ=1 AngleXU=0 Radius=0.67
    g23: Circle CenterX=80.2913 CenterY=-28.0488 CenterZ=0 NormalX=0 NormalY=0 NormalZ=1 AngleXU=0 Radius=0.63
    g24: Circle CenterX=99.0026 CenterY=-31.3481 CenterZ=0 NormalX=0 NormalY=0 NormalZ=1 AngleXU=0 Radius=0.635
    g25: Circle CenterX=117.714 CenterY=-34.6474 CenterZ=0 NormalX=0 NormalY=0 NormalZ=1 AngleXU=0 Radius=0.64
    g26: Circle CenterX=114.762 CenterY=-51.3891 CenterZ=0 NormalX=0 NormalY=0 NormalZ=1 AngleXU=0 Radius=0.69
    g27: Circle CenterX=96.0506 CenterY=-48.0898 CenterZ=0 NormalX=0 NormalY=0 NormalZ=1 AngleXU=0 Radius=0.685
    g28: Circle CenterX=77.3393 CenterY=-44.7905 CenterZ=0 NormalX=0 NormalY=0 NormalZ=1 AngleXU=0 Radius=0.68
    g29: Circle CenterX=83.7643 CenterY=-8.35261 CenterZ=0 NormalX=0 NormalY=0 NormalZ=1 AngleXU=0 Radius=0.58
    g30: Circle CenterX=102.476 CenterY=-11.6519 CenterZ=0 NormalX=0 NormalY=0 NormalZ=1 AngleXU=0 Radius=0.585
    g31: Circle CenterX=121.187 CenterY=-14.9512 CenterZ=0 NormalX=0 NormalY=0 NormalZ=1 AngleXU=0 Radius=0.59
    g32: Circle CenterX=124.139 CenterY=1.79049 CenterZ=0 NormalX=0 NormalY=0 NormalZ=1 AngleXU=0 Radius=0.54
    g33: Circle CenterX=105.428 CenterY=5.08981 CenterZ=0 NormalX=0 NormalY=0 NormalZ=1 AngleXU=0 Radius=0.535
    g34: Circle CenterX=86.7163 CenterY=8.38912 CenterZ=0 NormalX=0 NormalY=0 NormalZ=1 AngleXU=0 Radius=0.53
    g35: Circle CenterX=-27.4332 CenterY=-46.9208 CenterZ=0 NormalX=0 NormalY=0 NormalZ=1 AngleXU=0 Radius=0.66
    g36: Circle CenterX=-48 CenterY=-49 CenterZ=0 NormalX=0 NormalY=0 NormalZ=1 AngleXU=0 Radius=0.655
    g37: Circle CenterX=-66.5633 CenterY=-56.1619 CenterZ=0 NormalX=0 NormalY=0 NormalZ=1 AngleXU=0 Radius=0.65
    g38: Circle CenterX=-52.04 CenterY=-18.06 CenterZ=0 NormalX=0 NormalY=0 NormalZ=1 AngleXU=0 Radius=1.51
    g39: Circle CenterX=-58.39 CenterY=-18.06 CenterZ=0 NormalX=0 NormalY=0 NormalZ=1 AngleXU=0 Radius=1.505
    g40: Circle CenterX=-64.74 CenterY=-18.06 CenterZ=0 NormalX=0 NormalY=0 NormalZ=1 AngleXU=0 Radius=1.5
    g41: LineSegment StartX=-57.7066 StartY=-41.3167 StartZ=0 EndX=-56.2249 EndY=-58.2521 EndZ=0
    g42: LineSegment StartX=-56.2249 StartY=-58.2521 StartZ=0 EndX=-38.2934 EndY=-56.6833 EndZ=0
    g43: LineSegment StartX=-38.2934 StartY=-56.6833 StartZ=0 EndX=-34.8205 EndY=-36.9871 EndZ=0
    g44: LineSegment StartX=-20.0459 StartY=-56.8545 StartZ=0 EndX=-37.7725 EndY=-53.7288 EndZ=0
    g45: LineSegment StartX=-61.0132 StartY=-45.0964 StartZ=0 EndX=-55.1989 EndY=-61.0711 EndZ=0
    g46: LineSegment StartX=-55.1989 StartY=-61.0711 StartZ=0 EndX=-72.1133 EndY=-67.2275 EndZ=0
    g47: LineSegment StartX=86.7163 StartY=8.38912 StartZ=0 EndX=77.3393 EndY=-44.7905 EndZ=0
    g48: LineSegment StartX=105.428 StartY=5.08981 StartZ=0 EndX=96.0506 EndY=-48.0898 EndZ=0
    g49: LineSegment StartX=124.139 StartY=1.79049 StartZ=0 EndX=114.762 EndY=-51.3891 EndZ=0
    g50: LineSegment StartX=86.7163 StartY=8.38912 StartZ=0 EndX=124.139 EndY=1.79049 EndZ=0
    g51: LineSegment StartX=77.3393 StartY=-44.7905 StartZ=0 EndX=114.762 EndY=-51.3891 EndZ=0
    g52: GeomPoint X=100.739 Y=-21.5 Z=0
    g53: GeomPoint X=59.6127 Y=-41.6648 Z=0
    g54: GeomPoint X=74.3873 Y=-61.5322 Z=0
    g55: GeomPoint X=67 Y=-51.5985 Z=0
  constraints (155):
    c: Coincident(g1,g-1)
    c: PointOnObject(g2,g-2)
    c: PointOnObject(g3,g-2)
    c: Diameter(g1) = 1.12
    c: Diameter(g2) = 1.02
    c: DistanceY(g1,g2) = 17
    c: DistanceY(g3,g1) = 17
    c: Diameter(g3) = 1.22
    c: Diameter(g7) = 1
    c: Diameter(g4) = 1.01
    c: Diameter(g12) = 1.03
    c: Diameter(g16) = 1.04
    c: Diameter(g17) = 1.05
    c: Diameter(g34) = 1.06
    c: Diameter(g33) = 1.07
    c: Diameter(g32) = 1.08
    c: Diameter(g8) = 1.1
    c: Diameter(g5) = 1.11
    c: Diameter(g13) = 1.13
    c: Diameter(g15) = 1.14
    c: Diameter(g18) = 1.15
    c: Diameter(g29) = 1.16
    c: Diameter(g30) = 1.17
    c: Diameter(g31) = 1.18
    c: Diameter(g9) = 1.2
    c: Diameter(g6) = 1.21
    c: Diameter(g14) = 1.23
    c: Diameter(g19) = 1.24
    c: Diameter(g20) = 1.25
    c: Diameter(g23) = 1.26
    c: Diameter(g24) = 1.27
    c: Diameter(g25) = 1.28
    c: Diameter(g37) = 1.3
    c: Diameter(g36) = 1.31
    c: Diameter(g35) = 1.32
    c: Diameter(g22) = 1.34
    c: Diameter(g21) = 1.35
    c: Diameter(g28) = 1.36
    c: Diameter(g27) = 1.37
    c: Diameter(g26) = 1.38
    c: Diameter(g40) = 3
    c: Diameter(g39) = 3.01
    c: Diameter(g38) = 3.02
    c: Diameter(g0) = 0.5
    c: Diameter(g10) = 0.7
    c: Diameter(g11) = 0.6
    c: Vertical(g4,g5)
    c: Vertical(g5,g6)
    c: Vertical(g9,g8)
    c: Vertical(g8,g7)
    c: Vertical(g12,g13)
    c: Vertical(g13,g14)
    c: Vertical(g15,g16)
    c: DistanceY(g5,g4) = 17
    c: DistanceY(g6,g5) = 17
    c: DistanceY(g8,g7) = 17
    c: DistanceY(g9,g8) = 17
    c: DistanceY(g13,g12) = 17
    c: DistanceY(g14,g13) = 17
    c: DistanceY(g15,g16) = 17
    c: DistanceY(g22,g19) = 17
    c: DistanceY(g21,g20) = 17
    c: DistanceX(g19,g20) = 18
    c: DistanceX(g13,g15) = 18
    c: DistanceX(g1,g13) = 18
    c: DistanceX(g5,g1) = 20
    c: DistanceX(g8,g5) = 18
    c: DistanceY(g5,g1) = 8
    c: DistanceY(g8,g5) = 3
    c: DistanceY(g13,g1) = 10
    c: DistanceY(g15,g13) = 2
    c: DistanceX(g22,g21) = 18
    c: DistanceX(g1,g19) = 37
    c: DistanceY(g19,g1) = 31
    c: DistanceY(g20,g1) = 33
    c: DistanceX(g1,g22) = 35
    c: DistanceX(g0,g8) = 11.5
    c: DistanceX(g10,g0) = 8.89
    c: DistanceY(g10,g11) = 10.285
    c: DistanceX(g11,g10) = 12.44
    c: Horizontal(g38,g39)
    c: Horizontal(g39,g40)
    c: DistanceX(g39,g38) = 6.35
    c: DistanceX(g40,g39) = 6.35
    c: Vertical(g10,g39)
    c: DistanceY(g10,g0) = 16.51
    c: DistanceY(g39,g10) = 20.05
    c: DistanceX(g36,g1) = 48
    c: DistanceY(g36,g1) = 49
    c: Coincident(g42,g41)
    c: Coincident(g43,g42)
    c: PointOnObject(g44,g43)
    c: Coincident(g46,g45)
    c: PointOnObject(g41,g45)
    c: Perpendicular(g42,g41)
    c: Perpendicular(g45,g46)
    c: Perpendicular(g44,g43)
    c: Symmetric(g41,g42,g36)
    c: Symmetric(g43,g44,g35)
    c: Symmetric(g45,g46,g37)
    c: Distance(g42) = 18
    c: Distance(g44) = 18
    c: Distance(g46) = 18
    c: Distance(g45) = 17
    c: Distance(g41) = 17
    c: Distance(g43) = 20
    c: Distance(g41,g45) = 3
    c: Distance(g44,g42) = 3
    c: Angle(g-2,g41) = 0.0872665
    c: Angle(g43,g41) = 0.261799
    c: Angle(g41,g45) = 0.261799
    c: Coincident(g47,g34)
    c: Coincident(g47,g28)
    c: PointOnObject(g29,g47)
    c: Coincident(g48,g33)
    c: Coincident(g48,g27)
    c: PointOnObject(g24,g48)
    c: PointOnObject(g30,g48)
    c: Coincident(g49,g32)
    c: Coincident(g49,g26)
    c: PointOnObject(g25,g49)
    c: PointOnObject(g31,g49)
    c: Coincident(g50,g34)
    c: Coincident(g50,g32)
    c: Perpendicular(g50,g48)
    c: Perpendicular(g47,g50)
    c: Perpendicular(g49,g50)
    c: Symmetric(g34,g32,g33)
    c: Distance(g50) = 38
    c: Angle(g47,g-2) = 0.174533
    c: Distance(g47) = 54
    c: Distance(g29,g34) = 17
    c: Distance(g23,g28) = 17
    c: Distance(g27,g24) = 17
    c: Distance(g33,g30) = 17
    c: Distance(g32,g31) = 17
    c: Distance(g25,g26) = 17
    c: Coincident(g51,g28)
    c: Coincident(g51,g26)
    c: Perpendicular(g47,g51)
    c: PointOnObject(g27,g51)
    c: PointOnObject(g23,g47)
    c: Symmetric(g33,g27,g52)
    c: PointOnObject(g53,g51)
    c: PointOnObject(g54,g47)
    c: Distance(g28,g54) = 17
    c: Distance(g28,g53) = 18
    c: Symmetric(g53,g54,g55)
    c: DistanceX(g20,g55) = 12
    c: DistanceY(g1,g0) = 18.5
    c: DistanceY(g52,g1) = 21.5
    c: Vertical(g18,g20)
    c: DistanceY(g20,g18) = 17
    c: DistanceY(g18,g17) = 17
    c: DistanceX(g16,g17) = 18
